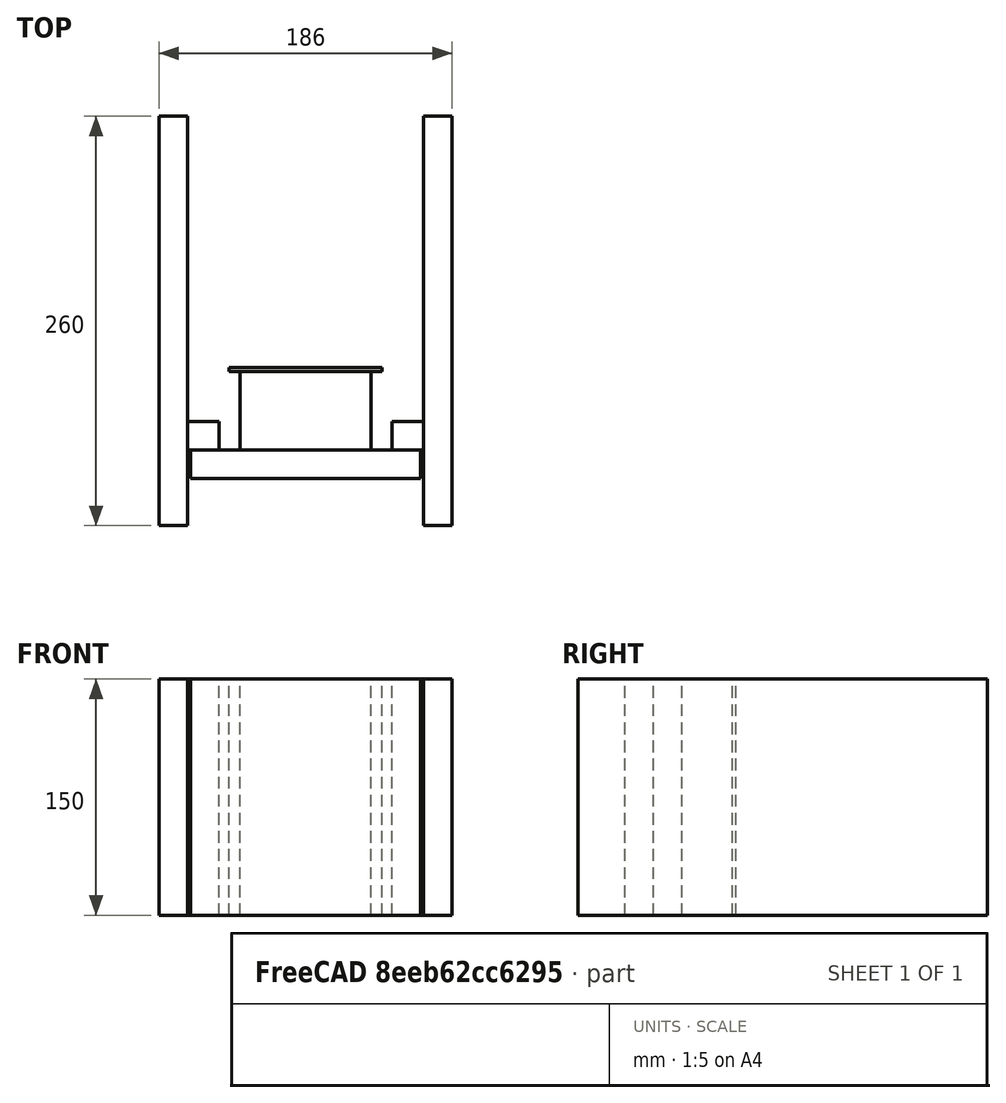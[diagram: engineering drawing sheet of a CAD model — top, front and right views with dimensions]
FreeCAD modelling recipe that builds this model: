
FCSTD DOCUMENT  (FreeCAD 0.19R24291 (Git))
Label: BoooooooomKoffer
License: All rights reserved
LicenseURL: http://en.wikipedia.org/wiki/All_rights_reserved
objects: Sketcher::SketchObject×2, Part::Extrusion×2, PartDesign::Body×1
note: 5 computed .brp shape members not serialized (recipe doc carries the construction recipe); baked Part::Feature solids carry a one-line shape summary decoded from their .brp

FEATURE [Sketcher::SketchObject] Sketch
  FullyConstrained = false
  MapMode = 5
  Support = -> [XY_Plane]
  sketch-geometry (41):
    g0: LineSegment StartX=0 StartY=130 StartZ=0 EndX=-18 EndY=130 EndZ=0
    g1: LineSegment StartX=-18 StartY=130 StartZ=0 EndX=-18 EndY=-130 EndZ=0
    g2: LineSegment StartX=-18 StartY=-130 StartZ=0 EndX=0 EndY=-130 EndZ=0
    g3: LineSegment StartX=0 StartY=-130 StartZ=0 EndX=0 EndY=130 EndZ=0
    g4: LineSegment StartX=168 StartY=130 StartZ=0 EndX=150 EndY=130 EndZ=0
    g5: LineSegment StartX=150 StartY=130 StartZ=0 EndX=150 EndY=-130 EndZ=0
    g6: LineSegment StartX=150 StartY=-130 StartZ=0 EndX=168 EndY=-130 EndZ=0
    g7: LineSegment StartX=168 StartY=-130 StartZ=0 EndX=168 EndY=130 EndZ=0
    g8: GeomPoint X=0 Y=0 Z=0
    g9: GeomPoint X=0 Y=0 Z=0
    g10: GeomPoint X=0 Y=0 Z=0
    g11: GeomPoint X=150 Y=0 Z=0
    g12: LineSegment StartX=0 StartY=0 StartZ=0 EndX=150 EndY=0 EndZ=0
    g13: GeomPoint X=0 Y=100 Z=0
    g14: GeomPoint X=150 Y=100 Z=0
    g15: GeomPoint X=0 Y=82 Z=0
    g16: GeomPoint X=150 Y=82 Z=0
    g17: LineSegment StartX=0 StartY=82 StartZ=0 EndX=20 EndY=82 EndZ=0
    g18: LineSegment StartX=20 StartY=82 StartZ=0 EndX=20 EndY=64 EndZ=0
    g19: LineSegment StartX=20 StartY=64 StartZ=0 EndX=0 EndY=64 EndZ=0
    g20: LineSegment StartX=0 StartY=64 StartZ=0 EndX=0 EndY=82 EndZ=0
    g21: LineSegment StartX=150 StartY=82 StartZ=0 EndX=130 EndY=82 EndZ=0
    g22: LineSegment StartX=130 StartY=82 StartZ=0 EndX=130 EndY=64 EndZ=0
    g23: LineSegment StartX=130 StartY=64 StartZ=0 EndX=150 EndY=64 EndZ=0
    g24: LineSegment StartX=150 StartY=64 StartZ=0 EndX=150 EndY=82 EndZ=0
    g25: LineSegment StartX=2 StartY=100 StartZ=0 EndX=148 EndY=100 EndZ=0
    g26: LineSegment StartX=148 StartY=100 StartZ=0 EndX=148 EndY=82 EndZ=0
    g27: LineSegment StartX=148 StartY=82 StartZ=0 EndX=2 EndY=82 EndZ=0
    g28: LineSegment StartX=2 StartY=82 StartZ=0 EndX=2 EndY=100 EndZ=0
    g29: LineSegment StartX=150 StartY=100 StartZ=0 EndX=148 EndY=100 EndZ=0
    g30: LineSegment StartX=2 StartY=100 StartZ=0 EndX=0 EndY=100 EndZ=0
    g31: LineSegment StartX=26.5 StartY=29.6 StartZ=0 EndX=123.5 EndY=29.6 EndZ=0
    g32: LineSegment StartX=123.5 StartY=29.6 StartZ=0 EndX=123.5 EndY=32 EndZ=0
    g33: LineSegment StartX=123.5 StartY=32 StartZ=0 EndX=26.5 EndY=32 EndZ=0
    g34: GeomPoint X=33.5 Y=32 Z=0
    g35: GeomPoint X=116.5 Y=32 Z=0
    g36: LineSegment StartX=33.5 StartY=32 StartZ=0 EndX=33.5 EndY=82 EndZ=0
    g37: LineSegment StartX=116.5 StartY=32 StartZ=0 EndX=116.5 EndY=82 EndZ=0
    g38: LineSegment StartX=116.5 StartY=82 StartZ=0 EndX=130 EndY=82 EndZ=0
    g39: LineSegment StartX=26.5 StartY=32 StartZ=0 EndX=26.5 EndY=29.6 EndZ=0
    g40: LineSegment StartX=123.5 StartY=29.6 StartZ=0 EndX=123.5 EndY=0 EndZ=0
  constraints (103):
    c: Coincident(g0,g1)
    c: Coincident(g1,g2)
    c: Coincident(g2,g3)
    c: Coincident(g3,g0)
    c: Horizontal(g0)
    c: Horizontal(g2)
    c: Vertical(g1)
    c: Vertical(g3)
    c: Coincident(g4,g5)
    c: Coincident(g5,g6)
    c: Coincident(g6,g7)
    c: Coincident(g7,g4)
    c: Horizontal(g4)
    c: Horizontal(g6)
    c: Vertical(g5)
    c: Vertical(g7)
    c: Distance(g2) = 18
    c: Distance(g6) = 18
    c: Distance(g0,g2) = 260
    c: Distance(g7) = 260
    c: PointOnObject(g8,g3)
    c: Coincident(g9,g8)
    c: Coincident(g10,g8)
    c: Distance(g8,g0) = 130
    c: PointOnObject(g11,g5)
    c: Distance(g11,g4) = 130
    c: Coincident(g12,g8)
    c: Coincident(g12,g11)
    c: Horizontal(g12)
    c: Distance(g12) = 150
    c: PointOnObject(g13,g3)
    c: PointOnObject(g14,g5)
    c: Distance(g13,g0) = 30
    c: Distance(g14,g4) = 30
    c: PointOnObject(g15,g3)
    c: PointOnObject(g16,g5)
    c: Distance(g15,g13) = 18
    c: Distance(g16,g14) = 18
    c: Coincident(g17,g18)
    c: Coincident(g18,g19)
    c: Coincident(g19,g20)
    c: Coincident(g20,g17)
    c: Horizontal(g17)
    c: Horizontal(g19)
    c: Vertical(g18)
    c: Vertical(g20)
    c: Coincident(g17,g15)
    c: Coincident(g21,g22)
    c: Coincident(g22,g23)
    c: Coincident(g23,g24)
    c: Coincident(g24,g21)
    c: Horizontal(g21)
    c: Horizontal(g23)
    c: Vertical(g22)
    c: Vertical(g24)
    c: Coincident(g21,g16)
    c: Distance(g17,g17) = 20
    c: Distance(g17,g18) = 18
    c: Distance(g21,g21) = 20
    c: Distance(g22,g21) = 18
    c: Coincident(g25,g26)
    c: Coincident(g26,g27)
    c: Coincident(g27,g28)
    c: Coincident(g28,g25)
    c: Horizontal(g25)
    c: Horizontal(g27)
    c: Vertical(g26)
    c: Vertical(g28)
    c: PointOnObject(g26,g21)
    c: Coincident(g29,g14)
    c: Coincident(g29,g25)
    c: Horizontal(g29)
    c: Distance(g29) = 2
    c: Coincident(g30,g25)
    c: Coincident(g30,g13)
    c: Distance(g30) = 2
    c: Coincident(g-1,g8)
    c: Coincident(g31,g32)
    c: Coincident(g32,g33)
    c: Horizontal(g31)
    c: Horizontal(g33)
    c: Vertical(g32)
    c: Distance(g32,g31) = 2.4
    c: Distance(g33) = 97
    c: Coincident(g36,g34)
    c: PointOnObject(g36,g27)
    c: Vertical(g36)
    c: Coincident(g37,g35)
    c: PointOnObject(g37,g27)
    c: Vertical(g37)
    c: Distance(g36) = 50
    c: PointOnObject(g37,g33)
    c: PointOnObject(g36,g33)
    c: Coincident(g38,g37)
    c: Distance(g37,g21) = 13.5
    c: Distance(g36,g33) = 7
    c: Distance(g37,g32) = 7
    c: Coincident(g39,g33)
    c: Coincident(g39,g31)
    c: Vertical(g39)
    c: Coincident(g40,g31)
    c: PointOnObject(g40,g12)
    c: Vertical(g40)
FEATURE [Sketcher::SketchObject] MirroredSketch
  FullyConstrained = false
  sketch-geometry (40):
    g0: LineSegment StartX=0 StartY=-130 StartZ=0 EndX=-18 EndY=-130 EndZ=0
    g1: LineSegment StartX=-18 StartY=-130 StartZ=0 EndX=-18 EndY=130 EndZ=0
    g2: LineSegment StartX=-18 StartY=130 StartZ=0 EndX=0 EndY=130 EndZ=0
    g3: LineSegment StartX=0 StartY=130 StartZ=0 EndX=0 EndY=-130 EndZ=0
    g4: LineSegment StartX=168 StartY=-130 StartZ=0 EndX=150 EndY=-130 EndZ=0
    g5: LineSegment StartX=150 StartY=-130 StartZ=0 EndX=150 EndY=130 EndZ=0
    g6: LineSegment StartX=150 StartY=130 StartZ=0 EndX=168 EndY=130 EndZ=0
    g7: LineSegment StartX=168 StartY=130 StartZ=0 EndX=168 EndY=-130 EndZ=0
    g8: GeomPoint X=0 Y=0 Z=0
    g9: GeomPoint X=0 Y=0 Z=0
    g10: GeomPoint X=0 Y=0 Z=0
    g11: GeomPoint X=150 Y=0 Z=0
    g12: LineSegment StartX=0 StartY=0 StartZ=0 EndX=150 EndY=0 EndZ=0
    g13: GeomPoint X=0 Y=-100 Z=0
    g14: GeomPoint X=150 Y=-100 Z=0
    g15: GeomPoint X=0 Y=-82 Z=0
    g16: GeomPoint X=150 Y=-82 Z=0
    g17: LineSegment StartX=0 StartY=-82 StartZ=0 EndX=20 EndY=-82 EndZ=0
    g18: LineSegment StartX=20 StartY=-82 StartZ=0 EndX=20 EndY=-64 EndZ=0
    g19: LineSegment StartX=20 StartY=-64 StartZ=0 EndX=0 EndY=-64 EndZ=0
    g20: LineSegment StartX=0 StartY=-64 StartZ=0 EndX=0 EndY=-82 EndZ=0
    g21: LineSegment StartX=150 StartY=-82 StartZ=0 EndX=130 EndY=-82 EndZ=0
    g22: LineSegment StartX=130 StartY=-82 StartZ=0 EndX=130 EndY=-64 EndZ=0
    g23: LineSegment StartX=130 StartY=-64 StartZ=0 EndX=150 EndY=-64 EndZ=0
    g24: LineSegment StartX=150 StartY=-64 StartZ=0 EndX=150 EndY=-82 EndZ=0
    g25: LineSegment StartX=2 StartY=-100 StartZ=0 EndX=148 EndY=-100 EndZ=0
    g26: LineSegment StartX=148 StartY=-100 StartZ=0 EndX=148 EndY=-82 EndZ=0
    g27: LineSegment StartX=148 StartY=-82 StartZ=0 EndX=2 EndY=-82 EndZ=0
    g28: LineSegment StartX=2 StartY=-82 StartZ=0 EndX=2 EndY=-100 EndZ=0
    g29: LineSegment StartX=150 StartY=-100 StartZ=0 EndX=148 EndY=-100 EndZ=0
    g30: LineSegment StartX=2 StartY=-100 StartZ=0 EndX=0 EndY=-100 EndZ=0
    g31: LineSegment StartX=26.5 StartY=-29.6 StartZ=0 EndX=123.5 EndY=-29.6 EndZ=0
    g32: LineSegment StartX=123.5 StartY=-29.6 StartZ=0 EndX=123.5 EndY=-32 EndZ=0
    g33: LineSegment StartX=123.5 StartY=-32 StartZ=0 EndX=26.5 EndY=-32 EndZ=0
    g34: GeomPoint X=33.5 Y=-32 Z=0
    g35: GeomPoint X=116.5 Y=-32 Z=0
    g36: LineSegment StartX=33.5 StartY=-32 StartZ=0 EndX=33.5 EndY=-82 EndZ=0
    g37: LineSegment StartX=116.5 StartY=-32 StartZ=0 EndX=116.5 EndY=-82 EndZ=0
    g38: LineSegment StartX=116.5 StartY=-82 StartZ=0 EndX=130 EndY=-82 EndZ=0
    g39: LineSegment StartX=26.5 StartY=-32 StartZ=0 EndX=26.5 EndY=-29.6 EndZ=0
  constraints (99):
    c: Coincident(g0,g1)
    c: Coincident(g1,g2)
    c: Coincident(g2,g3)
    c: Coincident(g3,g0)
    c: Horizontal(g0)
    c: Horizontal(g2)
    c: Vertical(g1)
    c: Vertical(g3)
    c: Coincident(g4,g5)
    c: Coincident(g5,g6)
    c: Coincident(g6,g7)
    c: Coincident(g7,g4)
    c: Horizontal(g4)
    c: Horizontal(g6)
    c: Vertical(g5)
    c: Vertical(g7)
    c: Distance(g2) = 18
    c: Distance(g6) = 18
    c: Distance(g0,g2) = 260
    c: Distance(g7) = 260
    c: PointOnObject(g8,g3)
    c: Coincident(g9,g8)
    c: Coincident(g10,g8)
    c: Distance(g8,g0) = 130
    c: PointOnObject(g11,g5)
    c: Distance(g11,g4) = 130
    c: Coincident(g12,g8)
    c: Coincident(g12,g11)
    c: Horizontal(g12)
    c: Distance(g12) = 150
    c: PointOnObject(g13,g3)
    c: PointOnObject(g14,g5)
    c: Distance(g13,g0) = 30
    c: Distance(g14,g4) = 30
    c: PointOnObject(g15,g3)
    c: PointOnObject(g16,g5)
    c: Distance(g15,g13) = 18
    c: Distance(g16,g14) = 18
    c: Coincident(g17,g18)
    c: Coincident(g18,g19)
    c: Coincident(g19,g20)
    c: Coincident(g20,g17)
    c: Horizontal(g17)
    c: Horizontal(g19)
    c: Vertical(g18)
    c: Vertical(g20)
    c: Coincident(g17,g15)
    c: Coincident(g21,g22)
    c: Coincident(g22,g23)
    c: Coincident(g23,g24)
    c: Coincident(g24,g21)
    c: Horizontal(g21)
    c: Horizontal(g23)
    c: Vertical(g22)
    c: Vertical(g24)
    c: Coincident(g21,g16)
    c: Distance(g17,g17) = 20
    c: Distance(g17,g18) = 18
    c: Distance(g21,g21) = 20
    c: Distance(g22,g21) = 18
    c: Coincident(g25,g26)
    c: Coincident(g26,g27)
    c: Coincident(g27,g28)
    c: Coincident(g28,g25)
    c: Horizontal(g25)
    c: Horizontal(g27)
    c: Vertical(g26)
    c: Vertical(g28)
    c: PointOnObject(g26,g21)
    c: Coincident(g29,g14)
    c: Coincident(g29,g25)
    c: Horizontal(g29)
    c: Distance(g29) = 2
    c: Coincident(g30,g25)
    c: Coincident(g30,g13)
    c: Distance(g30) = 2
    c: Coincident(g31,g32)
    c: Coincident(g32,g33)
    c: Horizontal(g31)
    c: Horizontal(g33)
    c: Vertical(g32)
    c: Distance(g32,g31) = 2.4
    c: Distance(g33) = 97
    c: Coincident(g36,g34)
    c: PointOnObject(g36,g27)
    c: Vertical(g36)
    c: Coincident(g37,g35)
    c: PointOnObject(g37,g27)
    c: Vertical(g37)
    c: Distance(g36) = 50
    c: PointOnObject(g37,g33)
    c: PointOnObject(g36,g33)
    c: Coincident(g38,g37)
    c: Distance(g37,g21) = 13.5
    c: Distance(g36,g33) = 7
    c: Distance(g37,g32) = 7
    c: Coincident(g39,g33)
    c: Coincident(g39,g31)
    c: Vertical(g39)
FEATURE [PartDesign::Body] Body
  Group = -> [Sketch,MirroredSketch]
  Origin = -> Origin
FEATURE [Part::Extrusion] Extrude
  Base = -> Sketch
  Dir = (0,0,1)
  DirMode = 2
  FaceMakerClass = Part::FaceMakerBullseye
  LengthFwd = 150
  LengthRev = 0
  Solid = false
  Symmetric = false
FEATURE [Part::Extrusion] Extrude001
  Base = -> MirroredSketch
  Dir = (0,0,1)
  DirMode = 2
  FaceMakerClass = Part::FaceMakerBullseye
  LengthFwd = 150
  LengthRev = 0
  Solid = false
  Symmetric = false
